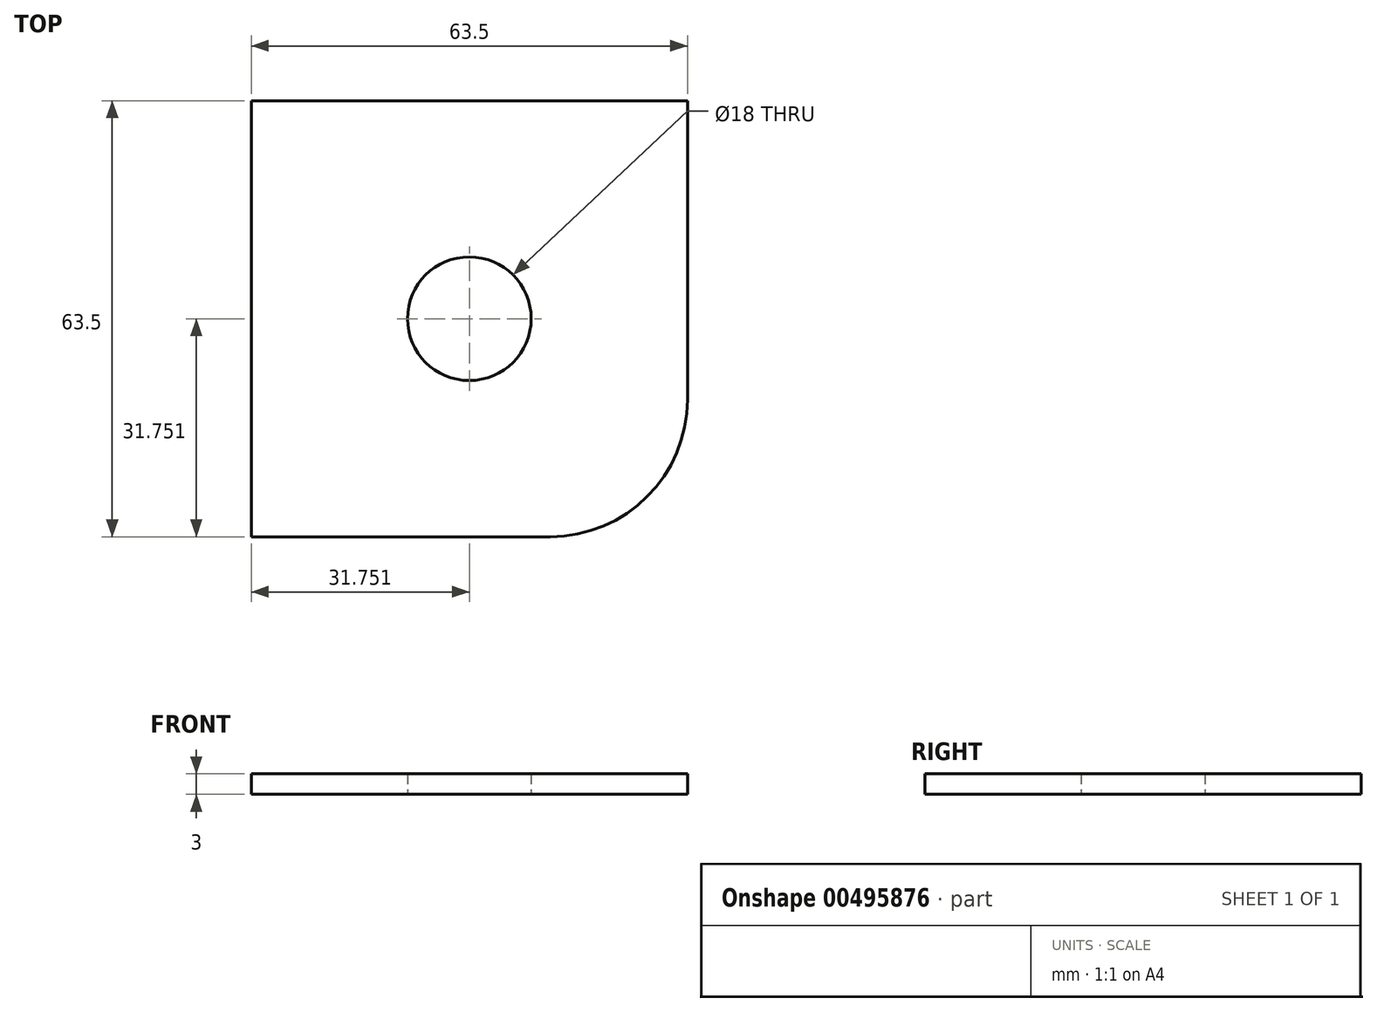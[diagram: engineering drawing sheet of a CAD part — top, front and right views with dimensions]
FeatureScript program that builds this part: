
annotation { "Feature Type Name" : "Feature", "Feature Type Description" : "" }
export const myFeature = defineFeature(function(context is Context, id is Id, definition is map)
    precondition{}
    {
        {
            var Q0;
            Q0=qCreatedBy(makeId("Top.planeOp"),FACE);
            var sketch = newSketch(context, id + "F0", { "sketchPlane" : qUnion([Q0])});
            skLineSegment(sketch, "E0.bottom", {"start": v(-27.08, 22.63) * mm, "end": v(36.42, 22.63) * mm});
            skLineSegment(sketch, "E0.top", {"start": v(-27.08, -40.87) * mm, "end": v(16.42, -40.87) * mm});
            skLineSegment(sketch, "E0.left", {"start": v(-27.08, 22.63) * mm, "end": v(-27.08, -40.87) * mm});
            skLineSegment(sketch, "E0.right", {"start": v(36.42, 22.63) * mm, "end": v(36.42, -20.87) * mm});
            skCircle(sketch, "E1", {"center": v(4.67, -9.12) * mm, "radius": 9 * mm});
            skArc(sketch, "E2", {"start": v(16.42, -40.87) * mm, "mid": v(30.56, -35.01) * mm, "end": v(36.42, -20.87) * mm});
            skPoint(sketch, "E3.orphan", {"position": v(36.42, -40.87) * mm});
            skSolve(sketch);
        }
        {
            var Q0;
            Q0 = qSketchRegion(id + "F0", true);
            extrude(context, id + "F1", {"entities" : qUnion([Q0]), "depth" : 3 * mm});
        }
    });
